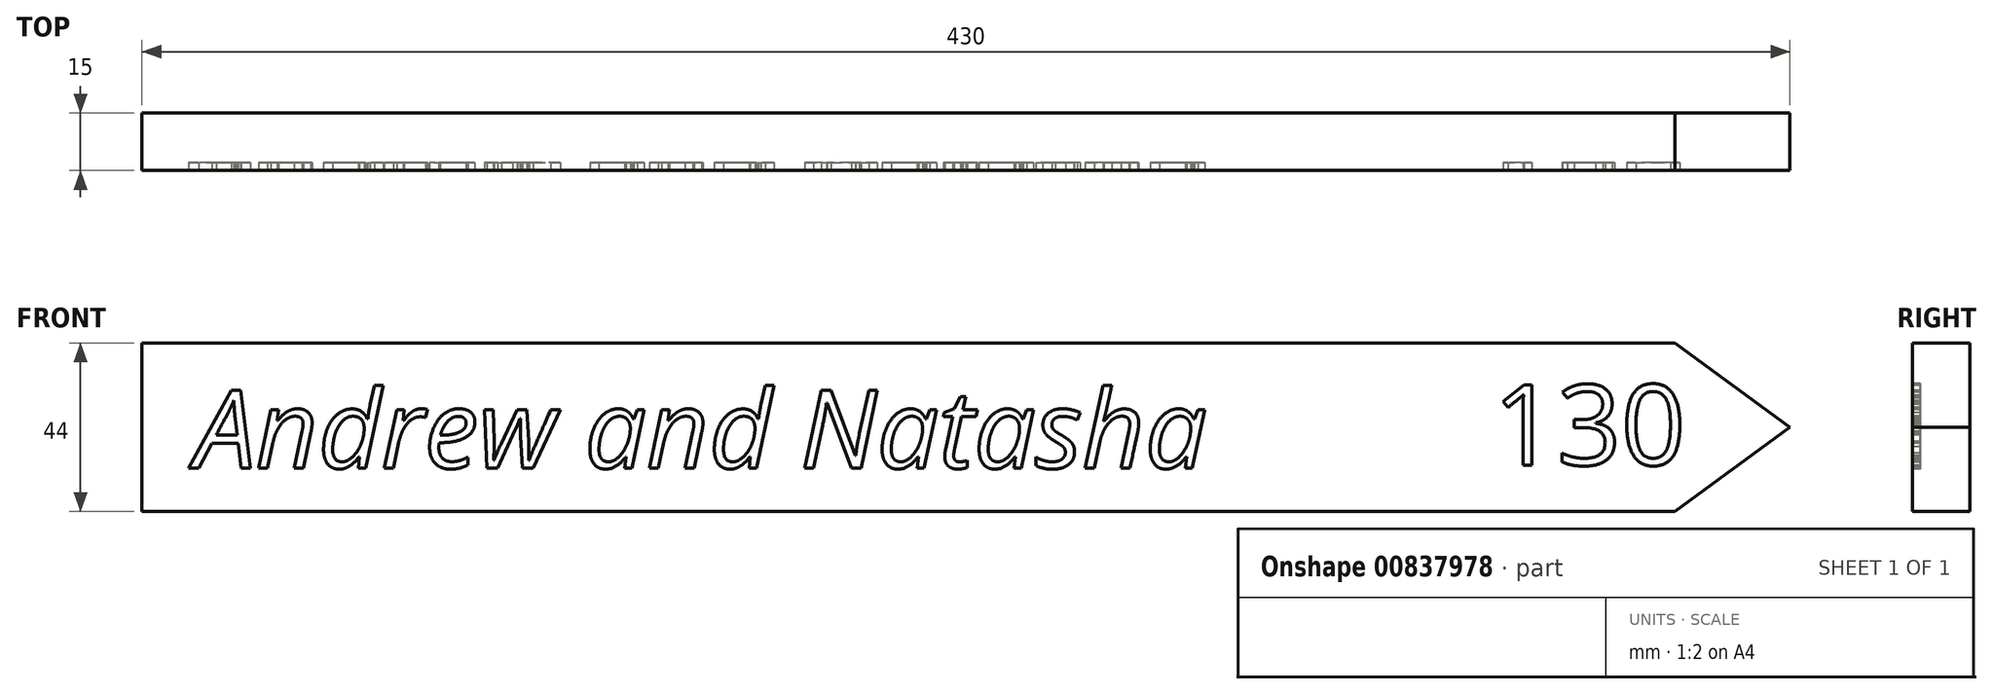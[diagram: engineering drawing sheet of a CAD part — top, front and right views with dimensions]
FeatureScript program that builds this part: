
annotation { "Feature Type Name" : "Feature", "Feature Type Description" : "" }
export const myFeature = defineFeature(function(context is Context, id is Id, definition is map)
    precondition{}
    {
        {
            var Q0;
            Q0=qCreatedBy(makeId("Front.planeOp"),FACE);
            var sketch = newSketch(context, id + "F0", { "sketchPlane" : qUnion([Q0])});
            skLineSegment(sketch, "E0.bottom", {"start": v(0, 0) * mm, "end": v(400, 0) * mm});
            skLineSegment(sketch, "E0.top", {"start": v(0, 44) * mm, "end": v(400, 44) * mm});
            skLineSegment(sketch, "E0.left", {"start": v(0, 0) * mm, "end": v(0, 44) * mm});
            skLineSegment(sketch, "E0.right", {"start": v(400, 0) * mm, "end": v(400, 44) * mm, "construction": true});
            skLineSegment(sketch, "E1", {"start": v(400, 22) * mm, "end": v(430, 22) * mm, "construction": true});
            skLineSegment(sketch, "E2", {"start": v(430, 22) * mm, "end": v(400, 44) * mm});
            skLineSegment(sketch, "E3", {"start": v(400, 0) * mm, "end": v(430, 22) * mm});
            skSolve(sketch);
        }
        {
            var Q0;
            Q0 = qSketchRegion(id + "F0", true);
            extrude(context, id + "F1", {"entities" : qUnion([Q0]), "depth" : 15 * mm, "offsetDistance" : 25 * mm});
        }
        {
            var Q0;
            Q0=makeQuery(id+"F1.opExtrude","CAP_FACE",FACE,{"disambiguationData":[OSD([sQuery(id+"F0.wireOp",EDGE,"E0.bottom"),sQuery(id+"F0.wireOp",EDGE,"E0.top"),sQuery(id+"F0.wireOp",EDGE,"E0.left"),sQuery(id+"F0.wireOp",EDGE,"E2"),sQuery(id+"F0.wireOp",EDGE,"E3")])],"isStart":false});
            var sketch = newSketch(context, id + "F2", { "sketchPlane" : qUnion([Q0])});
            skText(sketch, "E4", { "text": "Andrew and Natasha", "fontName": "OpenSans-Italic.ttf"});
            skText(sketch, "E5", { "text": "130", "fontName": "OpenSans-Regular.ttf"});
            const initialGuessF2  = {"E4": [0.01382, 0.0113, 1, 0, 0.02048], "E5": [0.35248, 0.01211, 1, 0, 0.0211]};
            skSetInitialGuess(sketch, initialGuessF2);
            skSolve(sketch);
        }
        {
            var Q0;
            Q0 = qSketchRegion(id + "F2", true);
            extrude(context, id + "F3", {"entities" : qUnion([Q0]), "operationType" : NewBodyOperationType.REMOVE, "oppositeDirection" : true, "depth" : 2 * mm, "offsetDistance" : 25 * mm});
        }
    });
